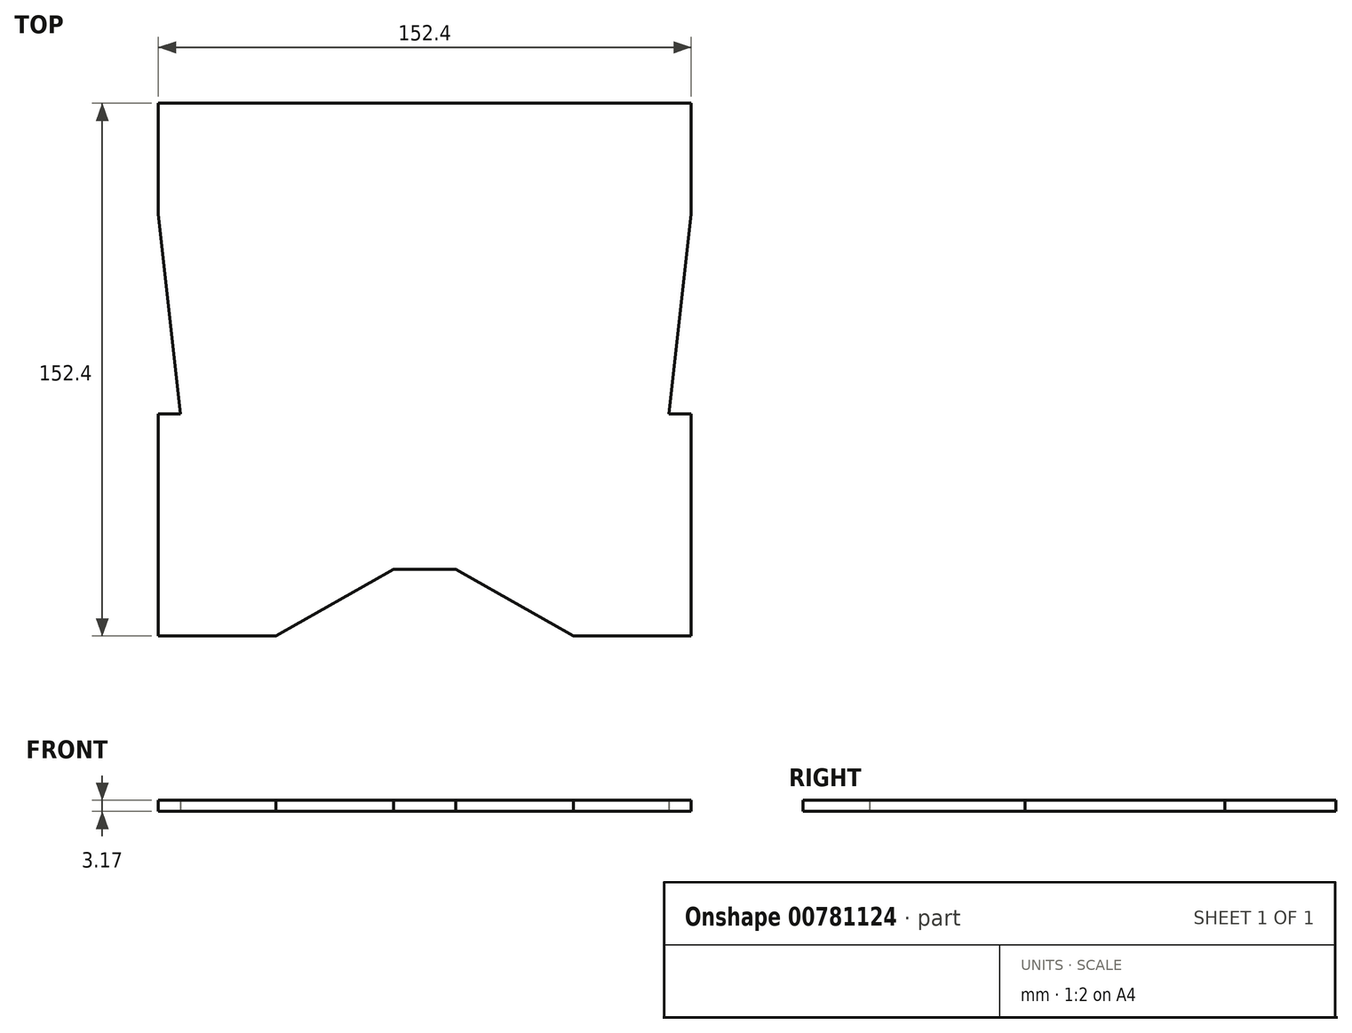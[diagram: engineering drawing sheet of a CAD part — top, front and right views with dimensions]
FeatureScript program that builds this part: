
annotation { "Feature Type Name" : "Feature", "Feature Type Description" : "" }
export const myFeature = defineFeature(function(context is Context, id is Id, definition is map)
    precondition{}
    {
        {
            var Q0;
            Q0=qCreatedBy(makeId("Top.planeOp"),FACE);
            var sketch = newSketch(context, id + "F0", { "sketchPlane" : qUnion([Q0])});
            skLineSegment(sketch, "E0.bottom", {"start": v(76.2, -76.2) * mm, "end": v(42.55, -76.2) * mm});
            skLineSegment(sketch, "E0.top", {"start": v(76.2, 76.2) * mm, "end": v(31.75, 76.2) * mm});
            skLineSegment(sketch, "E0.left", {"start": v(76.2, -76.2) * mm, "end": v(76.2, -12.7) * mm});
            skLineSegment(sketch, "E0.right", {"start": v(-76.2, -76.2) * mm, "end": v(-76.2, -12.7) * mm});
            skPoint(sketch, "E0.middle", {"position": v(0, 0) * mm});
            skLineSegment(sketch, "E1.bottom", {"start": v(-76.2, 76.2) * mm, "end": v(-31.75, 76.2) * mm});
            skLineSegment(sketch, "E1.left", {"start": v(-76.2, 76.2) * mm, "end": v(-76.2, 44.45) * mm});
            skLineSegment(sketch, "E2.left", {"start": v(76.2, 76.2) * mm, "end": v(76.2, 57.15) * mm});
            skLineSegment(sketch, "E3.trimOffspring", {"start": v(-31.75, 76.2) * mm, "end": v(-76.2, 76.2) * mm});
            skPoint(sketch, "E4", {"position": v(-76.2, -12.7) * mm});
            skLineSegment(sketch, "E5", {"start": v(-76.2, -12.7) * mm, "end": v(-69.85, -12.7) * mm});
            skLineSegment(sketch, "E6", {"start": v(-69.85, -12.7) * mm, "end": v(-76.2, 44.45) * mm});
            skLineSegment(sketch, "E7.trimOffspring", {"start": v(-76.2, 44.45) * mm, "end": v(-76.2, 76.2) * mm});
            skLineSegment(sketch, "E8.MirrorCS", {"start": v(69.85, -12.7) * mm, "end": v(76.2, 44.45) * mm});
            skLineSegment(sketch, "E9.MirrorCS", {"start": v(76.2, -12.7) * mm, "end": v(69.85, -12.7) * mm});
            skLineSegment(sketch, "E10.trimOffspring", {"start": v(76.2, 57.15) * mm, "end": v(76.2, 76.2) * mm});
            skLineSegment(sketch, "E11.top", {"start": v(-8.9, -57.15) * mm, "end": v(8.89, -57.15) * mm});
            skLineSegment(sketch, "E12.trimOffspring", {"start": v(-42.55, -76.2) * mm, "end": v(-76.2, -76.2) * mm});
            skLineSegment(sketch, "E13", {"start": v(76.2, 57.15) * mm, "end": v(76.2, 44.45) * mm});
            skLineSegment(sketch, "E14", {"start": v(-31.75, 76.2) * mm, "end": v(31.75, 76.2) * mm});
            skPoint(sketch, "E15", {"position": v(42.55, -76.2) * mm});
            skPoint(sketch, "E16", {"position": v(-42.55, -76.2) * mm});
            skLineSegment(sketch, "E17", {"start": v(8.89, -57.15) * mm, "end": v(42.55, -76.2) * mm});
            skLineSegment(sketch, "E18", {"start": v(-8.89, -57.15) * mm, "end": v(-42.55, -76.2) * mm});
            skSolve(sketch);
        }
        {
            var Q0;
            Q0=makeQuery(id+"F0.imprint","IMPRINT",FACE,{"disambiguationData":[TD([[makeQuery(id+"F0.imprint","IMPRINT",EDGE,{"derivedFrom":sQuery(id+"F0.wireOp",EDGE,"E0.bottom")}),-1.0]])]});
            extrude(context, id + "F1", {"entities" : qUnion([Q0]), "depth" : 3.17 * mm, "offsetDistance" : 25.4 * mm});
        }
    });
